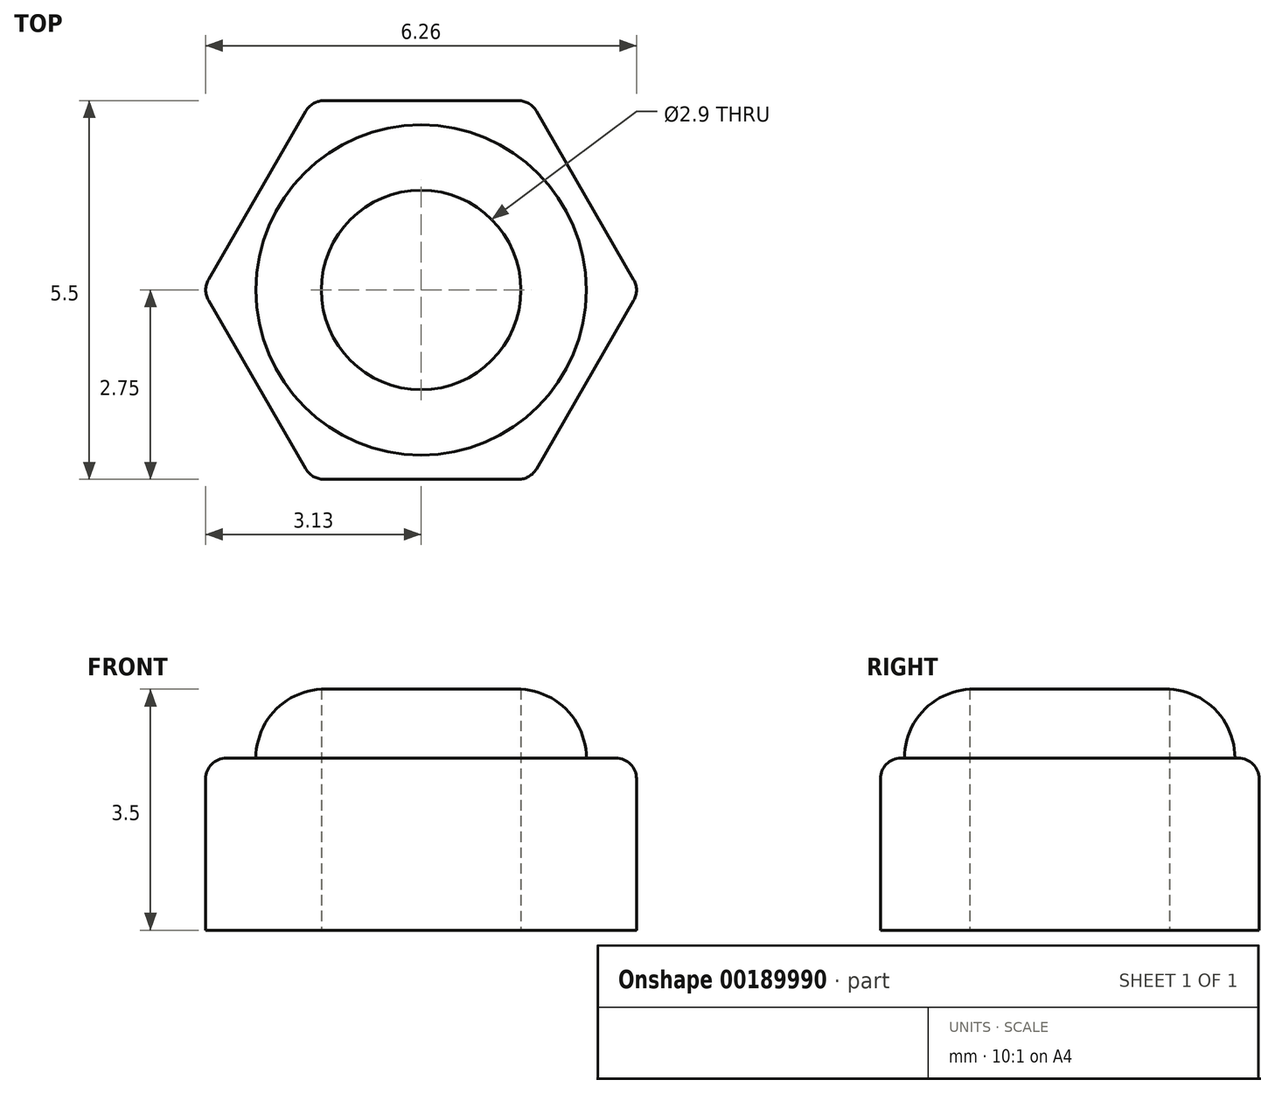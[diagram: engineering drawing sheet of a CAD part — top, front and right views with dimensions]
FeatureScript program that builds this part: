
annotation { "Feature Type Name" : "Feature", "Feature Type Description" : "" }
export const myFeature = defineFeature(function(context is Context, id is Id, definition is map)
    precondition{}
    {
        {
            var Q0;
            Q0=qCreatedBy(makeId("Top.planeOp"),FACE);
            var sketch = newSketch(context, id + "F0", { "sketchPlane" : qUnion([Q0])});
            skCircle(sketch, "E0", {"center": v(0, 0) * mm, "radius": 1.45 * mm});
            skCircle(sketch, "E1.cCircle", {"center": v(0, 0) * mm, "radius": 3.18 * mm, "construction": true});
            skLineSegment(sketch, "E1.0", {"start": v(1.59, -2.75) * mm, "end": v(-1.59, -2.75) * mm});
            skLineSegment(sketch, "E1.1", {"start": v(-1.59, -2.75) * mm, "end": v(-3.18, 0) * mm});
            skLineSegment(sketch, "E1.2", {"start": v(-3.18, 0) * mm, "end": v(-1.59, 2.75) * mm});
            skLineSegment(sketch, "E1.3", {"start": v(-1.59, 2.75) * mm, "end": v(1.59, 2.75) * mm});
            skLineSegment(sketch, "E1.4", {"start": v(1.59, 2.75) * mm, "end": v(3.18, 0) * mm});
            skLineSegment(sketch, "E1.5", {"start": v(3.18, 0) * mm, "end": v(1.59, -2.75) * mm});
            skSolve(sketch);
        }
        {
            var Q0;
            Q0 = qSketchRegion(id + "F0", true);
            extrude(context, id + "F1", {"entities" : qUnion([Q0]), "depth" : 2.5 * mm});
        }
        {
            var Q0;
            Q0=qCreatedBy(makeId("Top.planeOp"),FACE);
            cPlane(context, id + "F2", {"entities" : qUnion([Q0]), "cplaneType" : CPlaneType.OFFSET, "offset" : 2.5 * mm, "width" : 150 * mm, "height" : 150 * mm});
        }
        {
            var Q0;
            Q0=qCreatedBy(id+"F2.planeOp",FACE);
            var sketch = newSketch(context, id + "F3", { "sketchPlane" : qUnion([Q0])});
            skCircle(sketch, "E2", {"center": v(0, 0) * mm, "radius": 1.45 * mm});
            skCircle(sketch, "E3", {"center": v(0, 0) * mm, "radius": 2.4 * mm});
            skSolve(sketch);
        }
        {
            var Q0;
            Q0 = qSketchRegion(id + "F3", true);
            extrude(context, id + "F4", {"entities" : qUnion([Q0]), "operationType" : NewBodyOperationType.ADD, "depth" : 1 * mm});
        }
        {
            var Q0;
            Q0=makeQuery(id+"F1.opExtrude","CAP_EDGE",EDGE,{"disambiguationData":[OSD([sQuery(id+"F0.wireOp",EDGE,"E1.1")])],"isStart":false});
            var Q1;
            Q1=makeQuery(id+"F1.opExtrude","CAP_EDGE",EDGE,{"disambiguationData":[OSD([sQuery(id+"F0.wireOp",EDGE,"E1.2")])],"isStart":false});
            var Q2;
            Q2=makeQuery(id+"F1.opExtrude","CAP_EDGE",EDGE,{"disambiguationData":[OSD([sQuery(id+"F0.wireOp",EDGE,"E1.3")])],"isStart":false});
            var Q3;
            Q3=makeQuery(id+"F1.opExtrude","CAP_EDGE",EDGE,{"disambiguationData":[OSD([sQuery(id+"F0.wireOp",EDGE,"E1.4")])],"isStart":false});
            var Q4;
            Q4=makeQuery(id+"F1.opExtrude","CAP_EDGE",EDGE,{"disambiguationData":[OSD([sQuery(id+"F0.wireOp",EDGE,"E1.5")])],"isStart":false});
            var Q5;
            Q5=makeQuery(id+"F1.opExtrude","CAP_EDGE",EDGE,{"disambiguationData":[OSD([sQuery(id+"F0.wireOp",EDGE,"E1.0")])],"isStart":false});
            var Q6;
            Q6=makeQuery(id+"F1.opExtrude","SWEPT_EDGE",EDGE,{"disambiguationData":[OSD([sQuery(id+"F0.wireOp",EDGE,"E1.4"),sQuery(id+"F0.wireOp",EDGE,"E1.5")])]});
            var Q7;
            Q7=makeQuery(id+"F1.opExtrude","SWEPT_EDGE",EDGE,{"disambiguationData":[OSD([sQuery(id+"F0.wireOp",EDGE,"E1.3"),sQuery(id+"F0.wireOp",EDGE,"E1.4")])]});
            var Q8;
            Q8=makeQuery(id+"F1.opExtrude","SWEPT_EDGE",EDGE,{"disambiguationData":[OSD([sQuery(id+"F0.wireOp",EDGE,"E1.2"),sQuery(id+"F0.wireOp",EDGE,"E1.3")])]});
            var Q9;
            Q9=makeQuery(id+"F1.opExtrude","SWEPT_EDGE",EDGE,{"disambiguationData":[OSD([sQuery(id+"F0.wireOp",EDGE,"E1.1"),sQuery(id+"F0.wireOp",EDGE,"E1.2")])]});
            var Q10;
            Q10=makeQuery(id+"F1.opExtrude","SWEPT_EDGE",EDGE,{"disambiguationData":[OSD([sQuery(id+"F0.wireOp",EDGE,"E1.0"),sQuery(id+"F0.wireOp",EDGE,"E1.1")])]});
            var Q11;
            Q11=makeQuery(id+"F1.opExtrude","SWEPT_EDGE",EDGE,{"disambiguationData":[OSD([sQuery(id+"F0.wireOp",EDGE,"E1.0"),sQuery(id+"F0.wireOp",EDGE,"E1.5")])]});
            fillet(context, id + "F5", {"entities" : qUnion([Q0, Q1, Q2, Q3, Q4, Q5, Q6, Q7, Q8, Q9, Q10, Q11]), "radius" : .3 * mm, "tangentPropagation" : true, "allowEdgeOverflow" : false});
        }
        {
            var Q0;
            Q0=makeQuery(id+"F4.opExtrude","CAP_EDGE",EDGE,{"disambiguationData":[OSD([sQuery(id+"F3.wireOp",EDGE,"E3")])],"isStart":false});
            fillet(context, id + "F6", {"entities" : qUnion([Q0]), "radius" : 1 * mm, "tangentPropagation" : true, "allowEdgeOverflow" : false});
        }
    });
